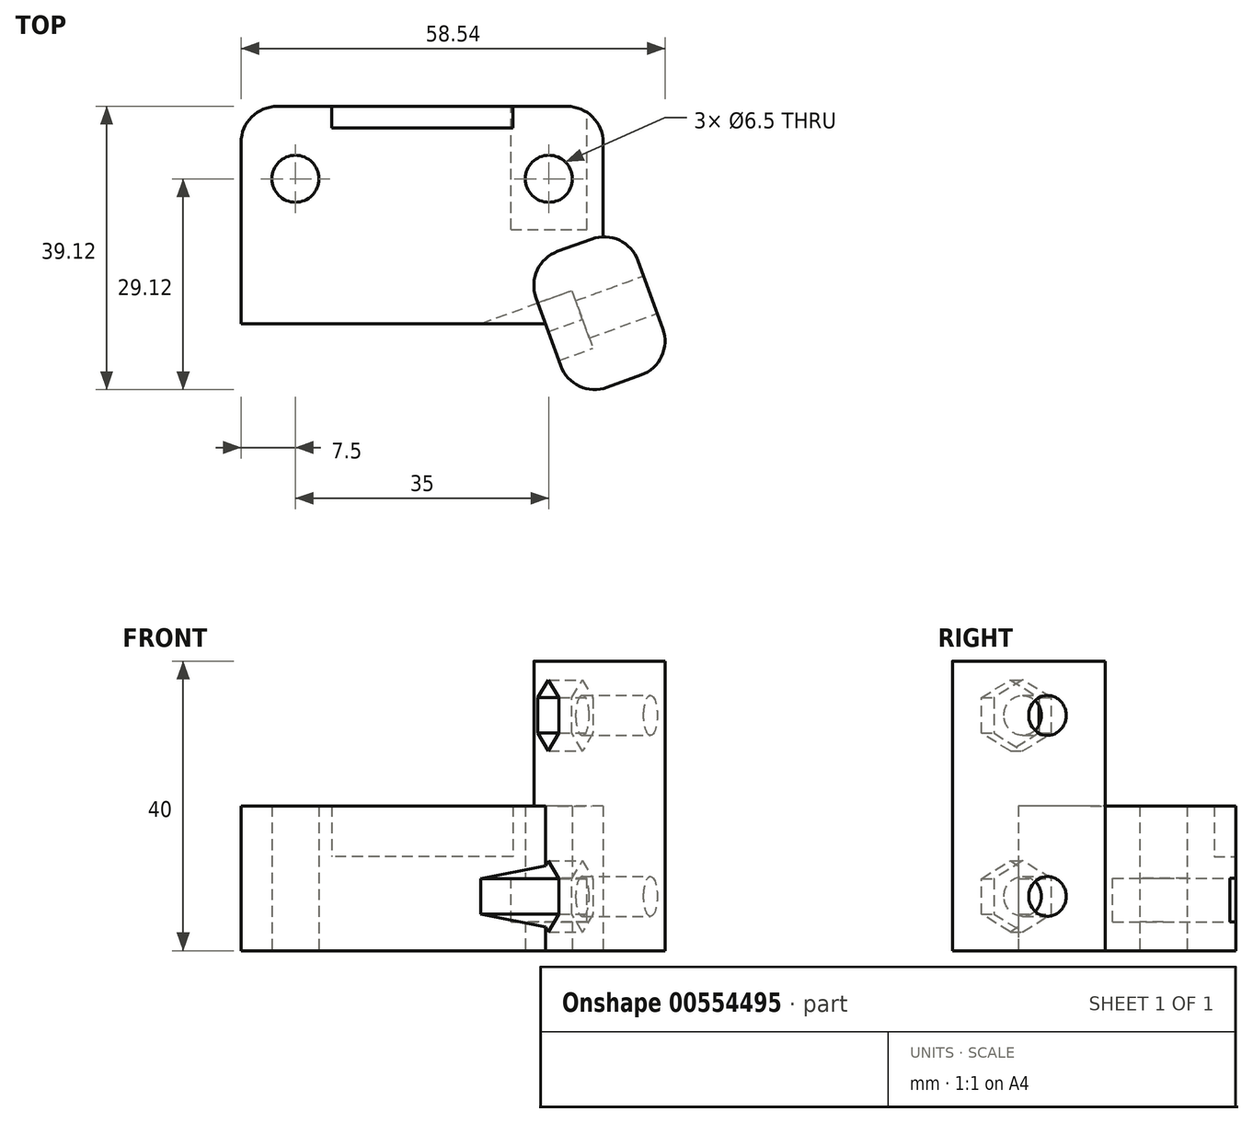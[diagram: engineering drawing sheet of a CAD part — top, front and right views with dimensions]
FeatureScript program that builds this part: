
annotation { "Feature Type Name" : "Feature", "Feature Type Description" : "" }
export const myFeature = defineFeature(function(context is Context, id is Id, definition is map)
    precondition{}
    {
        {
            var Q0;
            Q0=qCreatedBy(makeId("Top.planeOp"),FACE);
            var sketch = newSketch(context, id + "F0", { "sketchPlane" : qUnion([Q0])});
            skLineSegment(sketch, "E0.bottom", {"start": v(25, 15) * mm, "end": v(-25, 15) * mm});
            skLineSegment(sketch, "E0.top", {"start": v(25, -15) * mm, "end": v(-25, -15) * mm});
            skLineSegment(sketch, "E0.left", {"start": v(25, 15) * mm, "end": v(25, -15) * mm});
            skLineSegment(sketch, "E0.right", {"start": v(-25, 15) * mm, "end": v(-25, -15) * mm});
            skPoint(sketch, "E0.middle", {"position": v(0, 0) * mm});
            skSolve(sketch);
        }
        {
            var Q0;
            Q0=makeQuery(id+"F0.imprint","IMPRINT",FACE,{"disambiguationData":[TD([[makeQuery(id+"F0.imprint","IMPRINT",EDGE,{"derivedFrom":sQuery(id+"F0.wireOp",EDGE,"E0.bottom")}),1.0]])]});
            extrude(context, id + "F1", {"entities" : qUnion([Q0]), "depth" : 20 * mm, "offsetDistance" : 25 * mm});
        }
        {
            var Q0;
            Q0=makeQuery(id+"F1.opExtrude","CAP_FACE",FACE,{"disambiguationData":[OSD([sQuery(id+"F0.wireOp",EDGE,"E0.bottom"),sQuery(id+"F0.wireOp",EDGE,"E0.top"),sQuery(id+"F0.wireOp",EDGE,"E0.left"),sQuery(id+"F0.wireOp",EDGE,"E0.right")])],"isStart":true});
            var sketch = newSketch(context, id + "F2", { "sketchPlane" : qUnion([Q0])});
            skPoint(sketch, "E1", {"position": v(-17.5, -5) * mm});
            skPoint(sketch, "E2", {"position": v(17.5, -5) * mm});
            skSolve(sketch);
        }
        {
            var Q0;
            Q0=sQuery(id+"F2.wireOp",VERTEX,"E1");
            var Q1;
            Q1=sQuery(id+"F2.wireOp",VERTEX,"E2");
            var Q2;
            Q2=makeQuery(id+"F1.opExtrude","SWEPT_BODY",BODY,{"disambiguationData":[OSD([sQuery(id+"F0.wireOp",EDGE,"E0.bottom"),sQuery(id+"F0.wireOp",EDGE,"E0.top"),sQuery(id+"F0.wireOp",EDGE,"E0.left"),sQuery(id+"F0.wireOp",EDGE,"E0.right")])]});
            hole(context, id + "F3", {"style" : HoleStyle.SIMPLE, "endStyle" : HoleEndStyle.THROUGH, "holeDiameter" : 6.5 * mm, "isTappedThrough" : true, "tappedDepth" : 12 * mm, "tapClearance" : 3, "locations" : qUnion([Q0, Q1]), "scope" : qUnion([Q2])});
        }
        {
            var Q0;
            Q0=makeQuery(id+"F1.opExtrude","SWEPT_FACE",FACE,{"disambiguationData":[OSD([sQuery(id+"F0.wireOp",EDGE,"E0.bottom")])]});
            var sketch = newSketch(context, id + "F4", { "sketchPlane" : qUnion([Q0])});
            skLineSegment(sketch, "E3.bottom", {"start": v(-12.5, 20) * mm, "end": v(12.5, 20) * mm});
            skLineSegment(sketch, "E3.top", {"start": v(-12.5, 13) * mm, "end": v(12.5, 13) * mm});
            skLineSegment(sketch, "E3.left", {"start": v(-12.5, 20) * mm, "end": v(-12.5, 13) * mm});
            skLineSegment(sketch, "E3.right", {"start": v(12.5, 20) * mm, "end": v(12.5, 13) * mm});
            skPoint(sketch, "E4", {"position": v(0, 20) * mm});
            skSolve(sketch);
        }
        {
            var Q0;
            Q0=makeQuery(id+"F4.imprint","IMPRINT",FACE,{"disambiguationData":[TD([[makeQuery(id+"F4.imprint","IMPRINT",EDGE,{"derivedFrom":sQuery(id+"F4.wireOp",EDGE,"E3.bottom")}),-1.0]])]});
            extrude(context, id + "F5", {"entities" : qUnion([Q0]), "operationType" : NewBodyOperationType.REMOVE, "oppositeDirection" : true, "depth" : 3 * mm, "offsetDistance" : 25 * mm});
        }
        {
            var Q0;
            Q0=makeQuery(id+"F1.opExtrude","SWEPT_EDGE",EDGE,{"disambiguationData":[OSD([sQuery(id+"F0.wireOp",EDGE,"E0.top"),sQuery(id+"F0.wireOp",EDGE,"E0.left")])]});
            cPlane(context, id + "F6", {"entities" : qUnion([Q0]), "cplaneType" : CPlaneType.LINE_ANGLE, "offset" : 25 * mm, "angle" : 20 * degree, "oppositeDirection" : true, "width" : 150 * mm, "height" : 150 * mm});
        }
        {
            var Q0;
            Q0=qCreatedBy(id+"F6.planeOp",FACE);
            var sketch = newSketch(context, id + "F7", { "sketchPlane" : qUnion([Q0])});
            skLineSegment(sketch, "E5.bottom", {"start": v(11.12, 40) * mm, "end": v(31.12, 40) * mm});
            skLineSegment(sketch, "E5.top", {"start": v(11.12, 0) * mm, "end": v(31.12, 0) * mm});
            skLineSegment(sketch, "E5.left", {"start": v(11.12, 40) * mm, "end": v(11.12, 0) * mm});
            skLineSegment(sketch, "E5.right", {"start": v(31.12, 40) * mm, "end": v(31.12, 0) * mm});
            skSolve(sketch);
        }
        {
            var Q0;
            Q0=makeQuery(id+"F7.imprint","IMPRINT",FACE,{"disambiguationData":[TD([[makeQuery(id+"F7.imprint","IMPRINT",EDGE,{"derivedFrom":sQuery(id+"F7.wireOp",EDGE,"E5.bottom")}),-1.0]])]});
            extrude(context, id + "F8", {"entities" : qUnion([Q0]), "operationType" : NewBodyOperationType.ADD, "endBound" : BoundingType.SYMMETRIC, "depth" : 15 * mm, "offsetDistance" : 25 * mm});
        }
        {
            var Q0;
            Q0=makeQuery(id+"F8.opExtrude","CAP_FACE",FACE,{"disambiguationData":[OSD([sQuery(id+"F7.wireOp",EDGE,"E5.bottom"),sQuery(id+"F7.wireOp",EDGE,"E5.top"),sQuery(id+"F7.wireOp",EDGE,"E5.left"),sQuery(id+"F7.wireOp",EDGE,"E5.right")])],"isStart":true});
            var sketch = newSketch(context, id + "F9", { "sketchPlane" : qUnion([Q0])});
            skPoint(sketch, "E6", {"position": v(-21.12, 32.5) * mm});
            skPoint(sketch, "E7", {"position": v(-21.12, 7.5) * mm});
            skPoint(sketch, "E8", {"position": v(-21.12, 40) * mm});
            skSolve(sketch);
        }
        {
            var Q0;
            Q0=sQuery(id+"F9.wireOp",VERTEX,"E6");
            var Q1;
            Q1=sQuery(id+"F9.wireOp",VERTEX,"E7");
            var Q2;
            Q2=makeQuery(id+"F1.opExtrude","SWEPT_BODY",BODY,{"disambiguationData":[OSD([sQuery(id+"F0.wireOp",EDGE,"E0.bottom"),sQuery(id+"F0.wireOp",EDGE,"E0.top"),sQuery(id+"F0.wireOp",EDGE,"E0.left"),sQuery(id+"F0.wireOp",EDGE,"E0.right")])]});
            hole(context, id + "F10", {"style" : HoleStyle.SIMPLE, "endStyle" : HoleEndStyle.BLIND, "holeDiameter" : 5.5 * mm, "holeDepth" : 20 * mm, "isTappedThrough" : true, "tappedDepth" : 12 * mm, "tapClearance" : 3, "locations" : qUnion([Q0, Q1]), "scope" : qUnion([Q2])});
        }
        {
            var Q0;
            Q0=makeQuery(id+"F8.opExtrude","CAP_FACE",FACE,{"disambiguationData":[OSD([sQuery(id+"F7.wireOp",EDGE,"E5.bottom"),sQuery(id+"F7.wireOp",EDGE,"E5.top"),sQuery(id+"F7.wireOp",EDGE,"E5.left"),sQuery(id+"F7.wireOp",EDGE,"E5.right")])],"isStart":false});
            var sketch = newSketch(context, id + "F11", { "sketchPlane" : qUnion([Q0])});
            skCircle(sketch, "E9.cCircle", {"center": v(21.12, 32.5) * mm, "radius": 4.25 * mm, "construction": true});
            skLineSegment(sketch, "E9.0", {"start": v(21.12, 37.4) * mm, "end": v(25.37, 34.95) * mm});
            skLineSegment(sketch, "E9.1", {"start": v(25.37, 34.95) * mm, "end": v(25.37, 30.05) * mm});
            skLineSegment(sketch, "E9.2", {"start": v(25.37, 30.05) * mm, "end": v(21.12, 27.6) * mm});
            skLineSegment(sketch, "E9.3", {"start": v(21.12, 27.6) * mm, "end": v(16.87, 30.05) * mm});
            skLineSegment(sketch, "E9.4", {"start": v(16.87, 30.05) * mm, "end": v(16.87, 34.95) * mm});
            skLineSegment(sketch, "E9.5", {"start": v(16.87, 34.95) * mm, "end": v(21.12, 37.4) * mm});
            skPoint(sketch, "E9.0.midPoint", {"position": v(23.25, 36.18) * mm});
            skCircle(sketch, "E10.cCircle", {"center": v(21.12, 7.5) * mm, "radius": 4.25 * mm, "construction": true});
            skLineSegment(sketch, "E10.0", {"start": v(16.87, 5.05) * mm, "end": v(16.87, 9.95) * mm});
            skLineSegment(sketch, "E10.1", {"start": v(16.87, 9.95) * mm, "end": v(21.12, 12.4) * mm});
            skLineSegment(sketch, "E10.2", {"start": v(21.12, 12.4) * mm, "end": v(25.37, 9.95) * mm});
            skLineSegment(sketch, "E10.3", {"start": v(25.37, 9.95) * mm, "end": v(25.37, 5.05) * mm});
            skLineSegment(sketch, "E10.4", {"start": v(25.37, 5.05) * mm, "end": v(21.12, 2.6) * mm});
            skLineSegment(sketch, "E10.5", {"start": v(21.12, 2.6) * mm, "end": v(16.87, 5.05) * mm});
            skPoint(sketch, "E10.0.midPoint", {"position": v(16.87, 7.5) * mm});
            skSolve(sketch);
        }
        {
            var Q0;
            {var subQ0=makeQuery(id+"F8.opExtrude","CAP_FACE",FACE,{"disambiguationData":[OSD([sQuery(id+"F7.wireOp",EDGE,"E5.bottom"),sQuery(id+"F7.wireOp",EDGE,"E5.top"),sQuery(id+"F7.wireOp",EDGE,"E5.left"),sQuery(id+"F7.wireOp",EDGE,"E5.right")])],"isStart":false});var subQ1=makeQuery(id+"F10.hole-0.boolean.opBoolean","INTERSECT",EDGE,{"derivedFrom":[subQ0,makeQuery(id+"F10.hole-0.opRevolve","SWEPT_FACE",FACE,{"disambiguationData":[OSD([sQuery(id+"F10.hole-0.sketch.wireOp",EDGE,"core_line_2")])]})]});Q0=makeQuery(id+"F11.imprint","IMPRINT",FACE,{"disambiguationData":[TD([[makeQuery(id+"F11.imprint","IMPRINT",EDGE,{"derivedFrom":subQ1}),-1.0]])]});}
            var Q1;
            Q1=makeQuery(id+"F11.imprint","IMPRINT",FACE,{"disambiguationData":[TD([[makeQuery(id+"F11.imprint","IMPRINT",EDGE,{"derivedFrom":sQuery(id+"F11.wireOp",EDGE,"E9.0")}),-1.0]])]});
            var Q2;
            {var subQ0=makeQuery(id+"F8.opExtrude","CAP_FACE",FACE,{"disambiguationData":[OSD([sQuery(id+"F7.wireOp",EDGE,"E5.bottom"),sQuery(id+"F7.wireOp",EDGE,"E5.top"),sQuery(id+"F7.wireOp",EDGE,"E5.left"),sQuery(id+"F7.wireOp",EDGE,"E5.right")])],"isStart":false});var subQ1=makeQuery(id+"F10.hole-1.boolean.opBoolean","INTERSECT",EDGE,{"derivedFrom":[subQ0,makeQuery(id+"F10.hole-1.opRevolve","SWEPT_FACE",FACE,{"disambiguationData":[OSD([sQuery(id+"F10.hole-1.sketch.wireOp",EDGE,"core_line_2")])]})]});Q2=makeQuery(id+"F11.imprint","IMPRINT",FACE,{"disambiguationData":[TD([[makeQuery(id+"F11.imprint","IMPRINT",EDGE,{"derivedFrom":subQ1}),-1.0]])]});}
            var Q3;
            {var subQ0=sQuery(id+"F11.wireOp",EDGE,"E10.2");Q3=makeQuery(id+"F11.imprint","IMPRINT",FACE,{"disambiguationData":[TD([[makeQuery(id+"F11.imprint","IMPRINT",EDGE,{"derivedFrom":subQ0}),-1.0]])]});}
            extrude(context, id + "F12", {"entities" : qUnion([Q0, Q1, Q2, Q3]), "operationType" : NewBodyOperationType.REMOVE, "depth" : 10 * mm, "offsetDistance" : 25 * mm, "hasSecondDirection" : true, "secondDirectionOppositeDirection" : true, "secondDirectionDepth" : 5 * mm});
        }
        {
            var Q0;
            Q0 = qSketchRegion(id + "F11", true);
            extrude(context, id + "F13", {"entities" : qUnion([Q0]), "operationType" : NewBodyOperationType.REMOVE, "depth" : 20 * mm, "offsetDistance" : 25 * mm, "hasSecondDirection" : true, "secondDirectionOppositeDirection" : true, "secondDirectionDepth" : 5 * mm});
        }
        {
            var Q0;
            Q0=makeQuery(id+"F1.opExtrude","SWEPT_FACE",FACE,{"disambiguationData":[OSD([sQuery(id+"F0.wireOp",EDGE,"E0.bottom")])]});
            var sketch = newSketch(context, id + "F14", { "sketchPlane" : qUnion([Q0])});
            skLineSegment(sketch, "E11.bottom", {"start": v(-12.25, 4) * mm, "end": v(-22.75, 4) * mm});
            skLineSegment(sketch, "E11.top", {"start": v(-12.25, 10) * mm, "end": v(-22.75, 10) * mm});
            skLineSegment(sketch, "E11.left", {"start": v(-12.25, 4) * mm, "end": v(-12.25, 10) * mm});
            skLineSegment(sketch, "E11.right", {"start": v(-22.75, 4) * mm, "end": v(-22.75, 10) * mm});
            skPoint(sketch, "E12", {"position": v(-17.5, 10) * mm});
            skSolve(sketch);
        }
        {
            var Q0;
            Q0=makeQuery(id+"F14.imprint","IMPRINT",FACE,{"disambiguationData":[TD([[makeQuery(id+"F14.imprint","IMPRINT",EDGE,{"derivedFrom":sQuery(id+"F14.wireOp",EDGE,"E11.bottom")}),-1.0]])]});
            extrude(context, id + "F15", {"entities" : qUnion([Q0]), "operationType" : NewBodyOperationType.REMOVE, "oppositeDirection" : true, "depth" : 17 * mm, "offsetDistance" : 25 * mm});
        }
        {
            var Q0;
            Q0=makeQuery(id+"F8.opExtrude","CAP_EDGE",EDGE,{"disambiguationData":[OSD([sQuery(id+"F7.wireOp",EDGE,"E5.right")])],"isStart":true});
            var Q1;
            Q1=makeQuery(id+"FWoEyshg63QrjJi_1.1.F8.opExtrude","CAP_EDGE",EDGE,{"disambiguationData":[OSD([sQuery(id+"F7.wireOp",EDGE,"E5.right")])],"isStart":true});
            var Q2;
            Q2=makeQuery(id+"FWoEyshg63QrjJi_1.1.F8.opExtrude","CAP_EDGE",EDGE,{"disambiguationData":[OSD([sQuery(id+"F7.wireOp",EDGE,"E5.left")])],"isStart":true});
            var Q3;
            Q3=makeQuery(id+"F8.opExtrude","CAP_EDGE",EDGE,{"disambiguationData":[OSD([sQuery(id+"F7.wireOp",EDGE,"E5.left")])],"isStart":true});
            fillet(context, id + "F16", {"entities" : qUnion([Q0, Q1, Q2, Q3]), "radius" : 5 * mm, "tangentPropagation" : true, "allowEdgeOverflow" : false});
        }
        {
            var Q0;
            Q0=makeQuery(id+"F1.opExtrude","SWEPT_EDGE",EDGE,{"disambiguationData":[OSD([sQuery(id+"F0.wireOp",EDGE,"E0.bottom"),sQuery(id+"F0.wireOp",EDGE,"E0.left")])]});
            var Q1;
            Q1=makeQuery(id+"F1.opExtrude","SWEPT_EDGE",EDGE,{"disambiguationData":[OSD([sQuery(id+"F0.wireOp",EDGE,"E0.bottom"),sQuery(id+"F0.wireOp",EDGE,"E0.right")])]});
            var Q2;
            Q2=makeQuery(id+"F8.opExtrude","CAP_EDGE",EDGE,{"disambiguationData":[OSD([sQuery(id+"F7.wireOp",EDGE,"E5.left")])],"isStart":false});
            var Q3;
            Q3=makeQuery(id+"F8.opExtrude","CAP_EDGE",EDGE,{"disambiguationData":[OSD([sQuery(id+"F7.wireOp",EDGE,"E5.right")])],"isStart":false});
            var Q4;
            Q4=makeQuery(id+"FWoEyshg63QrjJi_1.1.F8.opExtrude","CAP_EDGE",EDGE,{"disambiguationData":[OSD([sQuery(id+"F7.wireOp",EDGE,"E5.right")])],"isStart":false});
            var Q5;
            Q5=makeQuery(id+"FWoEyshg63QrjJi_1.1.F8.opExtrude","CAP_EDGE",EDGE,{"disambiguationData":[OSD([sQuery(id+"F7.wireOp",EDGE,"E5.left")])],"isStart":false});
            fillet(context, id + "F17", {"entities" : qUnion([Q0, Q1, Q2, Q3, Q4, Q5]), "radius" : 5 * mm, "tangentPropagation" : true, "allowEdgeOverflow" : false});
        }
    });
